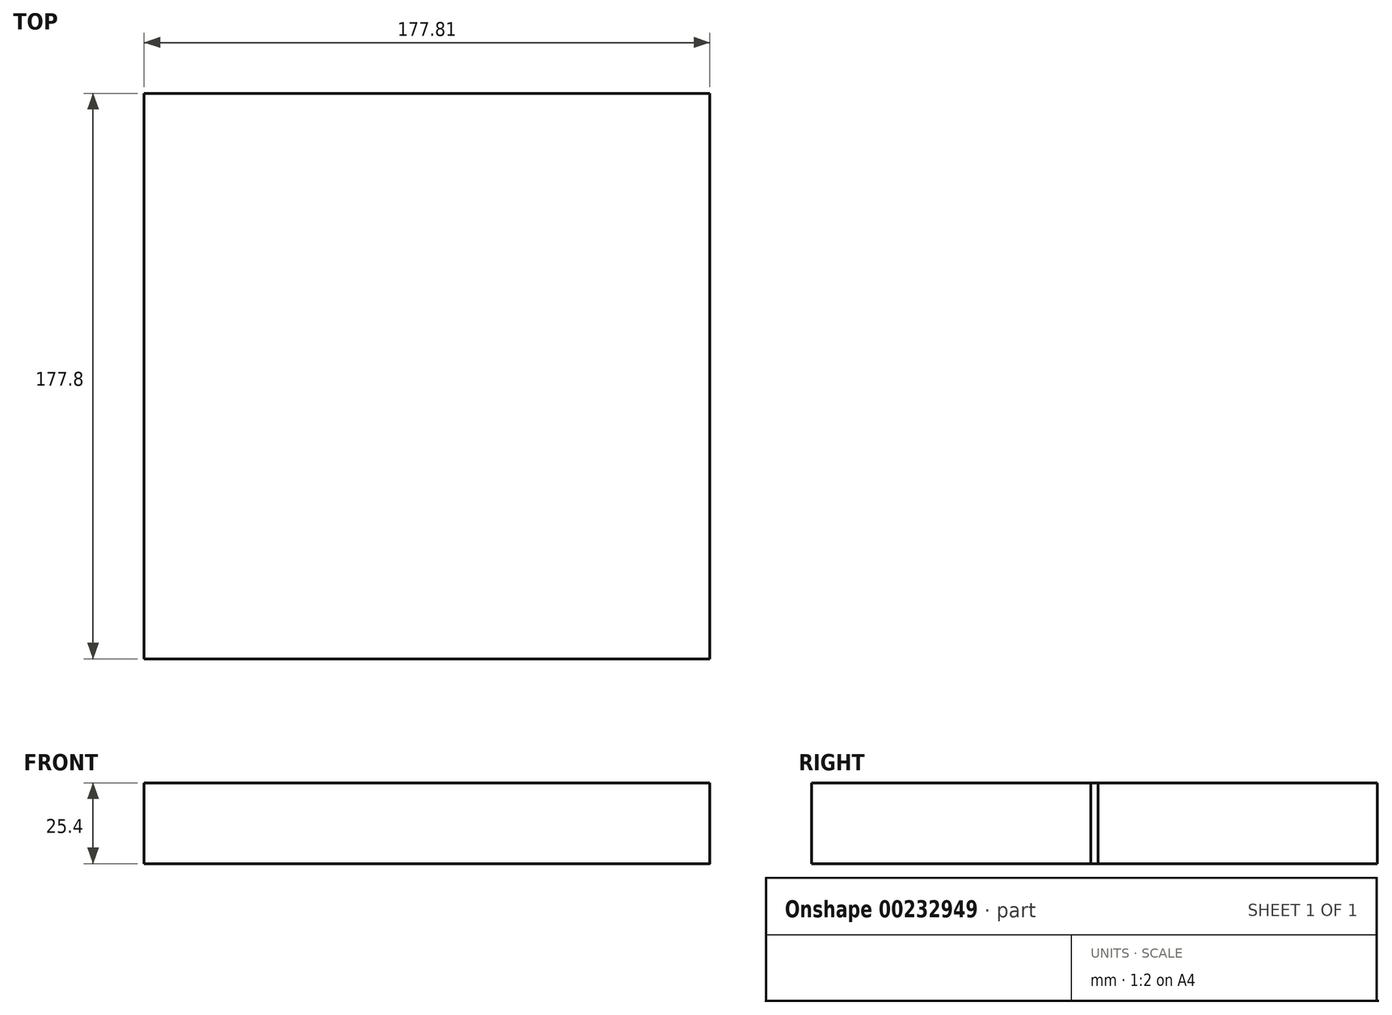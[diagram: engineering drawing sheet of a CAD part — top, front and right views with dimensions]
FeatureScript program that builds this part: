
annotation { "Feature Type Name" : "Feature", "Feature Type Description" : "" }
export const myFeature = defineFeature(function(context is Context, id is Id, definition is map)
    precondition{}
    {
        {
            var Q0;
            Q0=qCreatedBy(makeId("Top.planeOp"),FACE);
            var sketch = newSketch(context, id + "F0", { "sketchPlane" : qUnion([Q0])});
            skLineSegment(sketch, "E0.bottom", {"start": v(-78.24, 77.47) * mm, "end": v(99.56, 77.47) * mm});
            skLineSegment(sketch, "E0.top", {"start": v(-78.24, -100.33) * mm, "end": v(99.56, -100.33) * mm});
            skLineSegment(sketch, "E0.left", {"start": v(-78.24, 77.47) * mm, "end": v(-78.24, -100.33) * mm});
            skLineSegment(sketch, "E0.right", {"start": v(99.56, 77.47) * mm, "end": v(99.56, -100.33) * mm});
            skLineSegment(sketch, "E1", {"start": v(-78.24, 77.47) * mm, "end": v(-78.24, -11.43) * mm});
            skLineSegment(sketch, "E2", {"start": v(-78.24, -11.43) * mm, "end": v(-78.23, -11.43) * mm});
            skCircle(sketch, "E3", {"center": v(10.67, -11.43) * mm, "radius": 88.9 * mm});
            skSolve(sketch);
        }
        {
            var Q0;
            Q0 = qSketchRegion(id + "F0", true);
            extrude(context, id + "F1", {"entities" : qUnion([Q0]), "depth" : 25.4 * mm});
        }
    });
